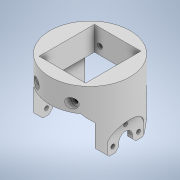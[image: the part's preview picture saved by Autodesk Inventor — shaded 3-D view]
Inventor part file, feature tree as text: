
AUTODESK INVENTOR PART (.ipt)
format: ipt  version: 2022 (Build 260153000, 153)  size: 303,616 bytes
history: native  units: mm
features: extrude x11, sketch x10, plane x4, mirror x1, chamfer x1
ambient origin geometry x8: Origin, YZ Plane, XZ Plane, XY Plane, X Axis, Y Axis, Z Axis, Center Point
bodies: Solid1 (feature_tree)
feature tree (27):
  extrude  "Extrusion1"  Depth=15.0mm TaperAngle=0.0deg
  extrude  "Extrusion2"  Depth=17.25mm
  extrude  "Extrusion3"  Depth=14.5mm
  plane  "Work Plane1"
  plane  "Work Plane2"
  extrude  "Extrusion4"  Depth=22.0mm
  extrude  "Extrusion5"  Depth=3.0mm
  plane  "Work Plane6"
  extrude  "Extrusion7"  Depth=10.0mm
  extrude  "Extrusion8"  Depth=10.0mm TaperAngle=0.0deg
  sketch  "Sketch24"  dims[d24=6.0mm d25=5.0mm d26=0.0mm]
  plane  "Work Plane7"
  extrude  "Extrusion14"  Depth=25.0mm
  extrude  "Extrusion15"  Depth=5.0mm TaperAngle=0.0deg
  mirror  "Mirror2"
  extrude  "Extrusion18"  Depth=4.7mm
  extrude  "Extrusion19"  Depth=4.7mm TaperAngle=0.0deg
  chamfer  "Chamfer5"  Distance=20.5mm
  sketch  "Sketch1"  dims[d0=50.0mm d1=15.0mm d2=0.0mm]
  sketch  "Sketch2"  dims[d3=34.5mm d4=17.25mm]
  sketch  "Sketch4"  dims[d5=29.0mm d6=14.5mm]
  sketch  "Sketch5"  dims[d7=50.0mm d8=0.0mm d13=22.0mm]
  sketch  "Sketch6"  dims[d14=3.5mm d15=3.0mm]
  sketch  "Sketch11"  dims[d16=3.0mm d17=10.0mm]
  sketch  "Sketch12"  dims[d18=10.0mm d19=100.0mm d20=0.0mm]
  sketch  "Sketch19"  dims[d21=-25.0mm d22=25.0mm d23=6.0mm]
  sketch  "Sketch25"  dims[d27=6.0mm d28=6.0mm d29=5.0mm d30=0.0mm d41=20.5mm d42=10.25mm d54=-25.0mm d58=20.5mm d62=50.0mm d63=0.0mm d64=80.0mm d65=100.0mm d66=0.0mm d67=-90.5mm d100=8.5mm d101=2.5mm d102=8.0mm d103=40.0mm d105=360.0deg d107=80.0mm d108=0.0mm d110=2.8mm d111=0.0mm d117=0.0mm d118=0.0mm d128=24.0mm d139=3.0mm d146=20.0mm d147=135.0deg d148=135.0deg d150=38.4mm d151=0.0mm d152=2.0mm d153=135.0deg d154=50.0mm d155=0.0mm d156=4.7mm d157=2.0mm d158=45.0deg]
